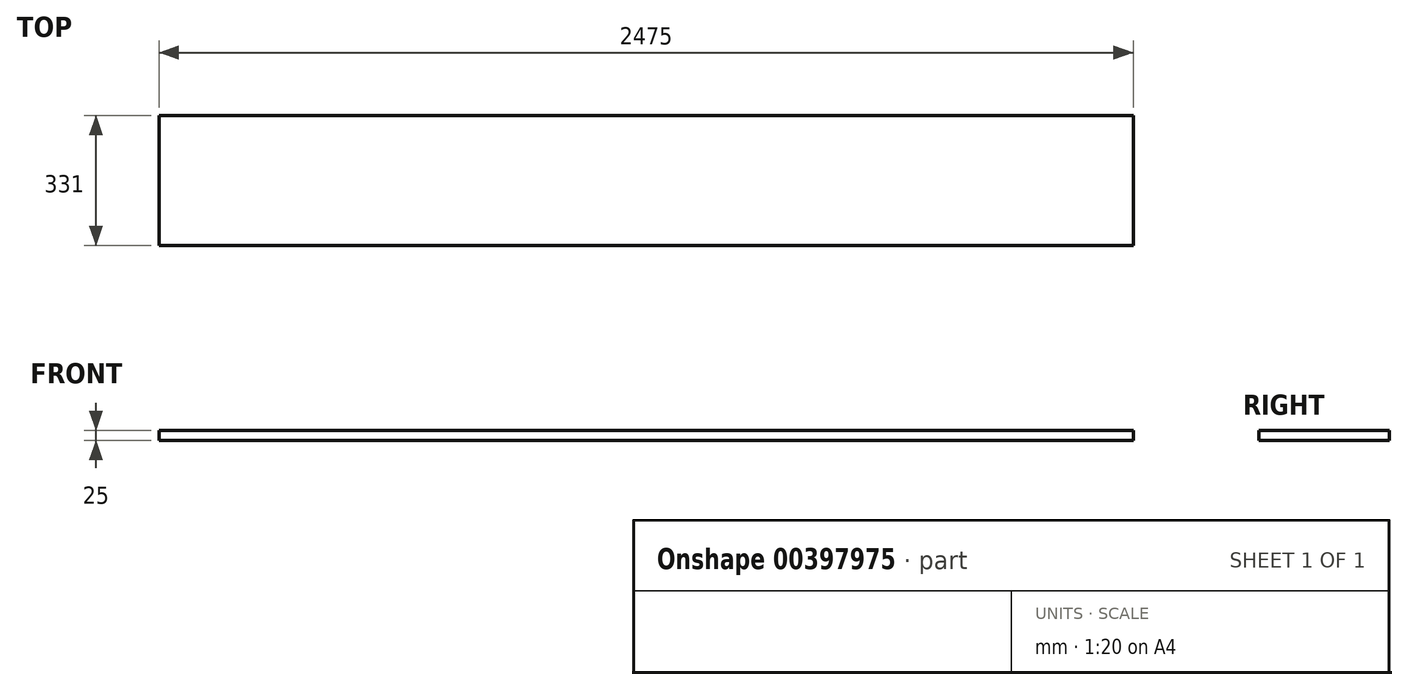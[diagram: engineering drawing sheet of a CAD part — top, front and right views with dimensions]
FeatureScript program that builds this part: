
annotation { "Feature Type Name" : "Feature", "Feature Type Description" : "" }
export const myFeature = defineFeature(function(context is Context, id is Id, definition is map)
    precondition{}
    {
        {
            var Q0;
            Q0=qCreatedBy(makeId("Front.planeOp"),FACE);
            var sketch = newSketch(context, id + "F0", { "sketchPlane" : qUnion([Q0])});
            skLineSegment(sketch, "E0.bottom", {"start": v(-1237.5, 12.5) * mm, "end": v(1237.5, 12.5) * mm});
            skLineSegment(sketch, "E0.top", {"start": v(-1237.5, -12.5) * mm, "end": v(1237.5, -12.5) * mm});
            skLineSegment(sketch, "E0.left", {"start": v(-1237.5, 12.5) * mm, "end": v(-1237.5, -12.5) * mm});
            skLineSegment(sketch, "E0.right", {"start": v(1237.5, 12.5) * mm, "end": v(1237.5, -12.5) * mm});
            skLineSegment(sketch, "E1", {"start": v(0, 12.5) * mm, "end": v(0, -12.5) * mm, "construction": true});
            skSolve(sketch);
        }
        {
            var Q0;
            Q0 = qSketchRegion(id + "F0", true);
            extrude(context, id + "F1", {"entities" : qUnion([Q0]), "depth" : 331 * mm});
        }
    });
